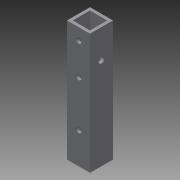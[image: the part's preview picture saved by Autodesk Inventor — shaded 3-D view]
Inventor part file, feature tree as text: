
AUTODESK INVENTOR PART (.ipt)
format: ipt  version: 2013 (Build 170138000, 138)  size: 111,104 bytes
history: native  units: in
note: dims shown in document units (in); Inventor stores cm internally (conversion verified against a paired STEP export)
features: extrude x4, sketch x4
ambient origin geometry x8: Origin, YZ Plane, XZ Plane, XY Plane, X Axis, Y Axis, Z Axis, Center Point
bodies: Solid1 (feature_tree)
feature tree (8):
  extrude  "Extrusion1"  Depth=5.25in
  extrude  "Extrusion2"  Depth=3.625in
  extrude  "Extrusion3"  TaperAngle=90.0deg  [1 undecoded]
  extrude  "Extrusion4"  Depth=2.0in
  sketch  "Sketch1"  dims[d0=1.0in d1=5.25in]
  sketch  "Sketch2"  dims[d2=1.0in d3=3.625in]
  sketch  "Sketch3"  dims[d4=3.375in d5=90.0deg]
  sketch  "Sketch4"  dims[d6=0.25in d7=2.0in d8=0.25in d9=1.0in d10=0.0in d11=0.75in d12=0.75in d13=10.0in d14=0.0in d15=1.25in d16=90.0deg d17=0.25in d18=10.0in d19=0.0in d20=0.5in d21=90.0deg d22=0.25in d23=1.0in d24=0.0in]
note: 1 required parameter value undecoded (feature->parameter linkage not recoverable at this tier; creation-order binding heuristic only, values carry confidence <= 0.55)
